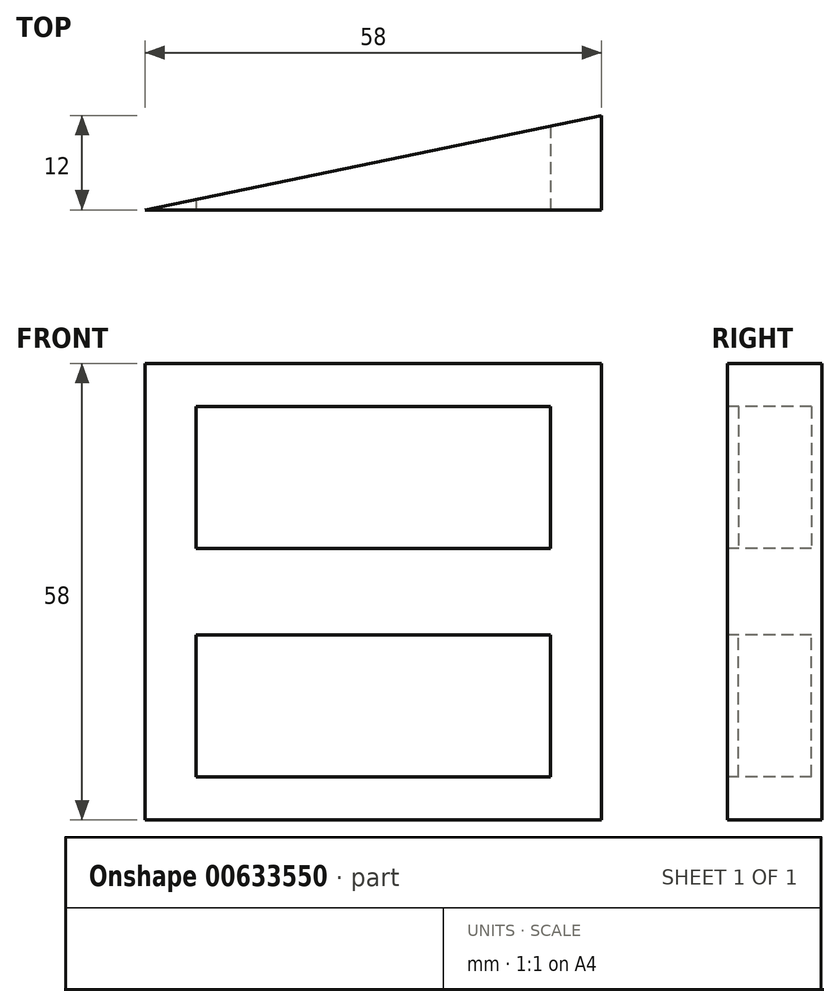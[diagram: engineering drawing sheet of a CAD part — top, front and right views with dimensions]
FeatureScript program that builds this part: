
annotation { "Feature Type Name" : "Feature", "Feature Type Description" : "" }
export const myFeature = defineFeature(function(context is Context, id is Id, definition is map)
    precondition{}
    {
        {
            var Q0;
            Q0=qCreatedBy(makeId("Top.planeOp"),FACE);
            var sketch = newSketch(context, id + "F0", { "sketchPlane" : qUnion([Q0])});
            skLineSegment(sketch, "E0", {"start": v(29, 6) * mm, "end": v(-29, -6) * mm});
            skLineSegment(sketch, "E1", {"start": v(-29, -6) * mm, "end": v(29, -6) * mm});
            skLineSegment(sketch, "E2", {"start": v(29, -6) * mm, "end": v(29, 6) * mm});
            skSolve(sketch);
        }
        {
            var Q0;
            Q0=makeQuery(id+"F0.imprint","IMPRINT",FACE,{"disambiguationData":[TD([[makeQuery(id+"F0.imprint","IMPRINT",EDGE,{"derivedFrom":sQuery(id+"F0.wireOp",EDGE,"E0")}),1.0]])]});
            extrude(context, id + "F1", {"entities" : qUnion([Q0]), "endBound" : BoundingType.SYMMETRIC, "depth" : 58 * mm, "offsetDistance" : 25 * mm});
        }
        {
            var Q0;
            Q0=makeQuery(id+"F1.opExtrude","SWEPT_FACE",FACE,{"disambiguationData":[OSD([sQuery(id+"F0.wireOp",EDGE,"E1")])]});
            var sketch = newSketch(context, id + "F2", { "sketchPlane" : qUnion([Q0])});
            skLineSegment(sketch, "E3.bottom", {"start": v(22.5, -23.5) * mm, "end": v(-22.5, -23.5) * mm});
            skLineSegment(sketch, "E3.top", {"start": v(22.5, -5.5) * mm, "end": v(-22.5, -5.5) * mm});
            skLineSegment(sketch, "E3.left", {"start": v(22.5, -23.5) * mm, "end": v(22.5, -5.5) * mm});
            skLineSegment(sketch, "E3.right", {"start": v(-22.5, -23.5) * mm, "end": v(-22.5, -5.5) * mm});
            skPoint(sketch, "E3.middle", {"position": v(0, -14.5) * mm});
            skLineSegment(sketch, "E4", {"start": v(0, 0) * mm, "end": v(0, -29) * mm, "construction": true});
            skLineSegment(sketch, "E5.MirrorCS", {"start": v(22.5, 23.5) * mm, "end": v(22.5, 5.5) * mm});
            skPoint(sketch, "E6.MirrorP", {"position": v(0, 14.5) * mm});
            skLineSegment(sketch, "E7.MirrorCS", {"start": v(22.5, 23.5) * mm, "end": v(-22.5, 23.5) * mm});
            skLineSegment(sketch, "E8.MirrorCS", {"start": v(-22.5, 23.5) * mm, "end": v(-22.5, 5.5) * mm});
            skLineSegment(sketch, "E9.MirrorCS", {"start": v(22.5, 5.5) * mm, "end": v(-22.5, 5.5) * mm});
            skSolve(sketch);
        }
        {
            var Q0;
            Q0=makeQuery(id+"F2.imprint","IMPRINT",FACE,{"disambiguationData":[TD([[makeQuery(id+"F2.imprint","IMPRINT",EDGE,{"derivedFrom":sQuery(id+"F2.wireOp",EDGE,"E3.bottom")}),-1.0]])]});
            var Q1;
            Q1=makeQuery(id+"F2.imprint","IMPRINT",FACE,{"disambiguationData":[TD([[makeQuery(id+"F2.imprint","IMPRINT",EDGE,{"derivedFrom":sQuery(id+"F2.wireOp",EDGE,"E5.MirrorCS")}),-1.0]])]});
            extrude(context, id + "F3", {"entities" : qUnion([Q0, Q1]), "operationType" : NewBodyOperationType.REMOVE, "endBound" : BoundingType.THROUGH_ALL, "oppositeDirection" : true, "depth" : 25 * mm, "offsetDistance" : 25 * mm});
        }
    });
